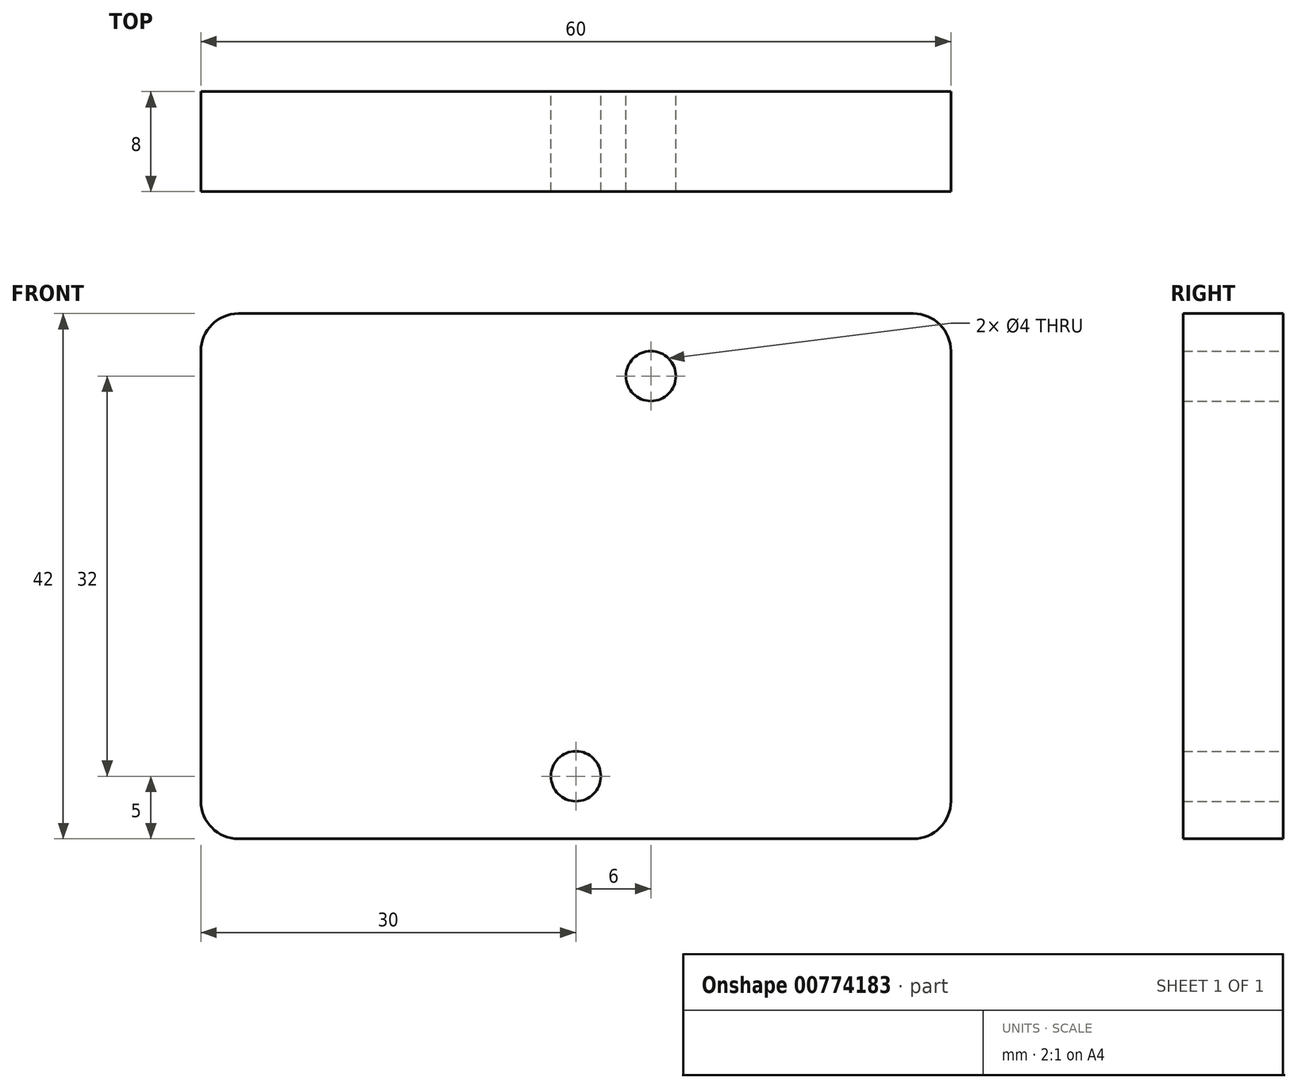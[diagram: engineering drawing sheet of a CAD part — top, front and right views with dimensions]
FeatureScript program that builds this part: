
annotation { "Feature Type Name" : "Feature", "Feature Type Description" : "" }
export const myFeature = defineFeature(function(context is Context, id is Id, definition is map)
    precondition{}
    {
        {
            var Q0;
            Q0=qCreatedBy(makeId("Front.planeOp"),FACE);
            var sketch = newSketch(context, id + "F0", { "sketchPlane" : qUnion([Q0])});
            skLineSegment(sketch, "E0.bottom", {"start": v(11.5, -11.5) * mm, "end": v(-11.5, -11.5) * mm});
            skLineSegment(sketch, "E0.top", {"start": v(11.5, 11.5) * mm, "end": v(-11.5, 11.5) * mm});
            skLineSegment(sketch, "E0.left", {"start": v(11.5, -11.5) * mm, "end": v(11.5, 11.5) * mm});
            skLineSegment(sketch, "E0.right", {"start": v(-11.5, -11.5) * mm, "end": v(-11.5, 11.5) * mm});
            skPoint(sketch, "E0.middle", {"position": v(0, 0) * mm});
            skLineSegment(sketch, "E1", {"start": v(11.5, 11.5) * mm, "end": v(11.5, 7.5) * mm});
            skLineSegment(sketch, "E2", {"start": v(11.5, 7.5) * mm, "end": v(16.5, 7.5) * mm});
            skLineSegment(sketch, "E3", {"start": v(16.5, 7.5) * mm, "end": v(16.5, 4.7) * mm});
            skLineSegment(sketch, "E4", {"start": v(16.5, 4.7) * mm, "end": v(11.5, 4.7) * mm});
            skLineSegment(sketch, "E5", {"start": v(-11.5, 11.5) * mm, "end": v(-11.5, 7.5) * mm});
            skLineSegment(sketch, "E6", {"start": v(-11.5, 7.5) * mm, "end": v(-16.5, 7.5) * mm});
            skLineSegment(sketch, "E7", {"start": v(-16.5, 7.5) * mm, "end": v(-16.5, 4.7) * mm});
            skLineSegment(sketch, "E8", {"start": v(-16.5, 4.7) * mm, "end": v(-11.5, 4.7) * mm});
            skSolve(sketch);
        }
        {
            var Q0;
            {var subQ2=sQuery(id+"F0.wireOp",EDGE,"E2");var subQ4=sQuery(id+"F0.wireOp",EDGE,"E0.bottom");var subQ11=sQuery(id+"F0.wireOp",EDGE,"E6");Q0=qUnion([makeQuery(id+"F0.imprint","IMPRINT",FACE,{"disambiguationData":[TD([[makeQuery(id+"F0.imprint","IMPRINT",EDGE,{"derivedFrom":subQ2}),-1.0]])]}),makeQuery(id+"F0.imprint","IMPRINT",FACE,{"disambiguationData":[TD([[makeQuery(id+"F0.imprint","IMPRINT",EDGE,{"derivedFrom":subQ11}),1.0]])]}),makeQuery(id+"F0.imprint","IMPRINT",FACE,{"disambiguationData":[TD([[makeQuery(id+"F0.imprint","IMPRINT",EDGE,{"derivedFrom":subQ4}),-1.0]])]})]);}
            extrude(context, id + "F1", {"entities" : qUnion([Q0]), "endBound" : BoundingType.SYMMETRIC, "depth" : 12.6 * mm, "offsetDistance" : 25 * mm});
        }
        {
            var Q0;
            Q0=qCreatedBy(makeId("Front.planeOp"),FACE);
            var sketch = newSketch(context, id + "F2", { "sketchPlane" : qUnion([Q0])});
            skLineSegment(sketch, "E9.bottom", {"start": v(23, -11.5) * mm, "end": v(-23, -11.5) * mm});
            skLineSegment(sketch, "E9.top", {"start": v(23, 11.5) * mm, "end": v(-23, 11.5) * mm});
            skLineSegment(sketch, "E9.left", {"start": v(23, -11.5) * mm, "end": v(23, 11.5) * mm});
            skLineSegment(sketch, "E9.right", {"start": v(-23, -11.5) * mm, "end": v(-23, 11.5) * mm});
            skPoint(sketch, "E9.middle", {"position": v(0, 0) * mm});
            skSolve(sketch);
        }
        {
            var Q0;
            Q0=qSketchRegion(id+"F2",true);
            extrude(context, id + "F3", {"entities" : qUnion([Q0]), "depth" : 16 * mm, "offsetDistance" : 25 * mm});
        }
        {
            var Q0;
            Q0=makeQuery(id+"F3.opExtrude","SWEPT_BODY",BODY,{"disambiguationData":[OSD([sQuery(id+"F2.wireOp",EDGE,"E9.bottom"),sQuery(id+"F2.wireOp",EDGE,"E9.top"),sQuery(id+"F2.wireOp",EDGE,"E9.left"),sQuery(id+"F2.wireOp",EDGE,"E9.right")])]});
            transform(context, id + "F4", {"entities" : qUnion([Q0]), "transformType" : TransformType.TRANSLATION_3D, "dx" : 0 * mm, "dy" : 9.75 * mm, "dz" : 0 * mm, "makeCopy" : false});
        }
        {
            var Q0;
            Q0=qCreatedBy(makeId("Front.planeOp"),FACE);
            var sketch = newSketch(context, id + "F5", { "sketchPlane" : qUnion([Q0])});
            skLineSegment(sketch, "E10", {"start": v(0, 0) * mm, "end": v(11.5, 0) * mm});
            skLineSegment(sketch, "E11", {"start": v(11.5, 0) * mm, "end": v(11.5, -4) * mm});
            skLineSegment(sketch, "E12", {"start": v(11.5, -4) * mm, "end": v(15.5, -4) * mm});
            skLineSegment(sketch, "E13", {"start": v(15.5, -4) * mm, "end": v(15.5, -11.5) * mm});
            skLineSegment(sketch, "E14", {"start": v(15.5, -11.5) * mm, "end": v(11.5, -11.5) * mm});
            skLineSegment(sketch, "E15", {"start": v(11.5, -11.5) * mm, "end": v(11.5, -4) * mm});
            skSolve(sketch);
        }
        {
            var Q0;
            Q0=qSketchRegion(id+"F5",true);
            extrude(context, id + "F6", {"entities" : qUnion([Q0]), "depth" : 25 * mm, "offsetDistance" : 25 * mm});
        }
        {
            var Q0;
            Q0=makeQuery(id+"F6.opExtrude","SWEPT_BODY",BODY,{"disambiguationData":[OSD([sQuery(id+"F5.wireOp",EDGE,"E12"),sQuery(id+"F5.wireOp",EDGE,"E13"),sQuery(id+"F5.wireOp",EDGE,"E14"),sQuery(id+"F5.wireOp",EDGE,"E15")])]});
            transform(context, id + "F7", {"entities" : qUnion([Q0]), "transformType" : TransformType.TRANSLATION_3D, "dx" : 0 * mm, "dy" : 4 * mm, "dz" : 0 * mm, "makeCopy" : false});
        }
        {
            var Q0;
            Q0=makeQuery(id+"F6.opExtrude","SWEPT_BODY",BODY,{"disambiguationData":[OSD([sQuery(id+"F5.wireOp",EDGE,"E12"),sQuery(id+"F5.wireOp",EDGE,"E13"),sQuery(id+"F5.wireOp",EDGE,"E14"),sQuery(id+"F5.wireOp",EDGE,"E15")])]});
            var Q1;
            Q1=makeQuery(id+"F1.opExtrude","SWEPT_BODY",BODY,{"disambiguationData":[OSD([sQuery(id+"F0.wireOp",EDGE,"E0.bottom"),sQuery(id+"F0.wireOp",EDGE,"E0.top"),sQuery(id+"F0.wireOp",EDGE,"E0.left"),sQuery(id+"F0.wireOp",EDGE,"E0.right"),sQuery(id+"F0.wireOp",EDGE,"E2"),sQuery(id+"F0.wireOp",EDGE,"E3"),sQuery(id+"F0.wireOp",EDGE,"E4"),sQuery(id+"F0.wireOp",EDGE,"E6"),sQuery(id+"F0.wireOp",EDGE,"E7"),sQuery(id+"F0.wireOp",EDGE,"E8")])]});
            var Q2;
            Q2=makeQuery(id+"F3.opExtrude","SWEPT_BODY",BODY,{"disambiguationData":[OSD([sQuery(id+"F2.wireOp",EDGE,"E9.bottom"),sQuery(id+"F2.wireOp",EDGE,"E9.top"),sQuery(id+"F2.wireOp",EDGE,"E9.left"),sQuery(id+"F2.wireOp",EDGE,"E9.right")])]});
            booleanBodies(context, id + "F8", {"operationType" : BooleanOperationType.SUBTRACTION, "tools" : qUnion([Q0, Q1]), "targets" : qUnion([Q2])});
        }
        {
            var Q0;
            Q0=makeQuery(id+"F3.opExtrude","CAP_EDGE",EDGE,{"disambiguationData":[OSD([sQuery(id+"F2.wireOp",EDGE,"E9.right")])],"isStart":false});
            var Q1;
            Q1=makeQuery(id+"F3.opExtrude","CAP_EDGE",EDGE,{"disambiguationData":[OSD([sQuery(id+"F2.wireOp",EDGE,"E9.left")])],"isStart":false});
            var Q2;
            Q2=makeQuery(id+"F3.opExtrude","SWEPT_EDGE",EDGE,{"disambiguationData":[OSD([sQuery(id+"F2.wireOp",EDGE,"E9.top"),sQuery(id+"F2.wireOp",EDGE,"E9.left")])]});
            var Q3;
            Q3=makeQuery(id+"F3.opExtrude","SWEPT_EDGE",EDGE,{"disambiguationData":[OSD([sQuery(id+"F2.wireOp",EDGE,"E9.top"),sQuery(id+"F2.wireOp",EDGE,"E9.right")])]});
            var Q4;
            {var subQ1=sQuery(id+"F2.wireOp",EDGE,"E9.right");var subQ2=sQuery(id+"F2.wireOp",EDGE,"E9.top");Q4=makeQuery(id+"F8.opBoolean","SPLIT",EDGE,{"disambiguationData":[TD([makeQuery(id+"F3.opExtrude","SWEPT_FACE",FACE,{"disambiguationData":[OSD([subQ1])]})])],"derivedFrom":makeQuery(id+"F3.opExtrude","CAP_EDGE",EDGE,{"disambiguationData":[OSD([subQ2])],"isStart":false})});}
            var Q5;
            {var subQ1=sQuery(id+"F2.wireOp",EDGE,"E9.left");var subQ2=sQuery(id+"F2.wireOp",EDGE,"E9.top");Q5=makeQuery(id+"F8.opBoolean","SPLIT",EDGE,{"disambiguationData":[TD([makeQuery(id+"F3.opExtrude","SWEPT_FACE",FACE,{"disambiguationData":[OSD([subQ1])]})])],"derivedFrom":makeQuery(id+"F3.opExtrude","CAP_EDGE",EDGE,{"disambiguationData":[OSD([subQ2])],"isStart":false})});}
            var Q6;
            Q6=makeQuery(id+"F3.opExtrude","SWEPT_EDGE",EDGE,{"disambiguationData":[OSD([sQuery(id+"F2.wireOp",EDGE,"E9.bottom"),sQuery(id+"F2.wireOp",EDGE,"E9.left")])]});
            var Q7;
            {var subQ0=sQuery(id+"F2.wireOp",EDGE,"E9.bottom");var subQ1=sQuery(id+"F2.wireOp",EDGE,"E9.left");Q7=makeQuery(id+"F8.opBoolean","SPLIT",EDGE,{"disambiguationData":[TD([makeQuery(id+"F3.opExtrude","SWEPT_FACE",FACE,{"disambiguationData":[OSD([subQ1])]})])],"derivedFrom":makeQuery(id+"F3.opExtrude","CAP_EDGE",EDGE,{"disambiguationData":[OSD([subQ0])],"isStart":false})});}
            var Q8;
            Q8=makeQuery(id+"F3.opExtrude","SWEPT_EDGE",EDGE,{"disambiguationData":[OSD([sQuery(id+"F2.wireOp",EDGE,"E9.bottom"),sQuery(id+"F2.wireOp",EDGE,"E9.right")])]});
            var Q9;
            {var subQ1=sQuery(id+"F2.wireOp",EDGE,"E9.bottom");var subQ2=sQuery(id+"F2.wireOp",EDGE,"E9.right");Q9=makeQuery(id+"F8.opBoolean","SPLIT",EDGE,{"disambiguationData":[TD([makeQuery(id+"F3.opExtrude","SWEPT_FACE",FACE,{"disambiguationData":[OSD([subQ2])]})])],"derivedFrom":makeQuery(id+"F3.opExtrude","CAP_EDGE",EDGE,{"disambiguationData":[OSD([subQ1])],"isStart":false})});}
            fillet(context, id + "F9", {"entities" : qUnion([Q0, Q1, Q2, Q3, Q4, Q5, Q6, Q7, Q8, Q9]), "radius" : 1.5 * mm, "tangentPropagation" : true, "allowEdgeOverflow" : false});
        }
        {
            var Q0;
            Q0=qCreatedBy(makeId("Front.planeOp"),FACE);
            var sketch = newSketch(context, id + "F10", { "sketchPlane" : qUnion([Q0])});
            skLineSegment(sketch, "E16.bottom", {"start": v(23, -21) * mm, "end": v(-23, -21) * mm});
            skLineSegment(sketch, "E16.top", {"start": v(23, 21) * mm, "end": v(-23, 21) * mm});
            skLineSegment(sketch, "E16.left", {"start": v(23, -21) * mm, "end": v(23, 21) * mm});
            skLineSegment(sketch, "E16.right", {"start": v(-23, -21) * mm, "end": v(-23, 21) * mm});
            skPoint(sketch, "E16.middle", {"position": v(0, 0) * mm});
            skLineSegment(sketch, "E17", {"start": v(0, 0) * mm, "end": v(0, 16) * mm});
            skLineSegment(sketch, "E18", {"start": v(0, 16) * mm, "end": v(18, 16) * mm});
            skLineSegment(sketch, "E19", {"start": v(0, 16) * mm, "end": v(-18, 16) * mm});
            skLineSegment(sketch, "E20", {"start": v(0, 0) * mm, "end": v(0, -16) * mm});
            skLineSegment(sketch, "E21", {"start": v(0, -16) * mm, "end": v(18, -16) * mm});
            skLineSegment(sketch, "E22", {"start": v(0, -16) * mm, "end": v(-18, -16) * mm});
            skLineSegment(sketch, "E23", {"start": v(-18, 16) * mm, "end": v(-18, 18) * mm});
            skLineSegment(sketch, "E24", {"start": v(18, 16) * mm, "end": v(18, 14) * mm});
            skLineSegment(sketch, "E25", {"start": v(-18, -16) * mm, "end": v(-18, -14) * mm});
            skLineSegment(sketch, "E26", {"start": v(18, -16) * mm, "end": v(18, -18) * mm});
            skArc(sketch, "E27", {"start": v(-18, 18) * mm, "mid": v(-20, 16) * mm, "end": v(-18, 14) * mm});
            skArc(sketch, "E28", {"start": v(18, 14) * mm, "mid": v(20, 16) * mm, "end": v(18, 18) * mm});
            skArc(sketch, "E29", {"start": v(-18, -14) * mm, "mid": v(-20, -16) * mm, "end": v(-18, -18) * mm});
            skArc(sketch, "E30", {"start": v(18, -18) * mm, "mid": v(20, -16) * mm, "end": v(18, -14) * mm});
            skLineSegment(sketch, "E31", {"start": v(-18, 18) * mm, "end": v(18, 18) * mm});
            skLineSegment(sketch, "E32", {"start": v(-18, 14) * mm, "end": v(18, 14) * mm});
            skLineSegment(sketch, "E33", {"start": v(-18, -14) * mm, "end": v(18, -14) * mm});
            skLineSegment(sketch, "E34", {"start": v(-18, -18) * mm, "end": v(18, -18) * mm});
            skSolve(sketch);
        }
        {
            var Q0;
            Q0=qSketchRegion(id+"F10",true);
            extrude(context, id + "F11", {"entities" : qUnion([Q0]), "depth" : 3 * mm, "offsetDistance" : 25 * mm});
        }
        {
            var Q0;
            Q0=makeQuery(id+"F11.opExtrude","SWEPT_BODY",BODY,{"disambiguationData":[OSD([sQuery(id+"F10.wireOp",EDGE,"E16.bottom"),sQuery(id+"F10.wireOp",EDGE,"E16.top"),sQuery(id+"F10.wireOp",EDGE,"E16.left"),sQuery(id+"F10.wireOp",EDGE,"E16.right"),sQuery(id+"F10.wireOp",EDGE,"E27"),sQuery(id+"F10.wireOp",EDGE,"E28"),sQuery(id+"F10.wireOp",EDGE,"E29"),sQuery(id+"F10.wireOp",EDGE,"E30"),sQuery(id+"F10.wireOp",EDGE,"E31"),sQuery(id+"F10.wireOp",EDGE,"E32"),sQuery(id+"F10.wireOp",EDGE,"E33"),sQuery(id+"F10.wireOp",EDGE,"E34")])]});
            transform(context, id + "F12", {"entities" : qUnion([Q0]), "transformType" : TransformType.TRANSLATION_3D, "dx" : 0 * mm, "dy" : 12 * mm, "dz" : 0 * mm, "makeCopy" : false});
        }
        {
            var Q0;
            Q0=makeQuery(id+"F11.opExtrude","SWEPT_EDGE",EDGE,{"disambiguationData":[OSD([sQuery(id+"F10.wireOp",EDGE,"E16.top"),sQuery(id+"F10.wireOp",EDGE,"E16.right")])]});
            var Q1;
            Q1=makeQuery(id+"F11.opExtrude","SWEPT_EDGE",EDGE,{"disambiguationData":[OSD([sQuery(id+"F10.wireOp",EDGE,"E16.top"),sQuery(id+"F10.wireOp",EDGE,"E16.left")])]});
            var Q2;
            Q2=makeQuery(id+"F11.opExtrude","SWEPT_EDGE",EDGE,{"disambiguationData":[OSD([sQuery(id+"F10.wireOp",EDGE,"E16.bottom"),sQuery(id+"F10.wireOp",EDGE,"E16.left")])]});
            var Q3;
            Q3=makeQuery(id+"F11.opExtrude","SWEPT_EDGE",EDGE,{"disambiguationData":[OSD([sQuery(id+"F10.wireOp",EDGE,"E16.bottom"),sQuery(id+"F10.wireOp",EDGE,"E16.right")])]});
            fillet(context, id + "F13", {"entities" : qUnion([Q0, Q1, Q2, Q3]), "radius" : 3 * mm, "tangentPropagation" : true, "allowEdgeOverflow" : false});
        }
        {
            var Q0;
            Q0=qCreatedBy(makeId("Front.planeOp"),FACE);
            var sketch = newSketch(context, id + "F14", { "sketchPlane" : qUnion([Q0])});
            skLineSegment(sketch, "E35.bottom", {"start": v(30, -21) * mm, "end": v(-30, -21) * mm});
            skLineSegment(sketch, "E35.top", {"start": v(30, 21) * mm, "end": v(-30, 21) * mm});
            skLineSegment(sketch, "E35.left", {"start": v(30, -21) * mm, "end": v(30, 21) * mm});
            skLineSegment(sketch, "E35.right", {"start": v(-30, -21) * mm, "end": v(-30, 21) * mm});
            skPoint(sketch, "E35.middle", {"position": v(0, 0) * mm});
            skLineSegment(sketch, "E36", {"start": v(0, 0) * mm, "end": v(0, 16) * mm});
            skLineSegment(sketch, "E37", {"start": v(0, 0) * mm, "end": v(0, -16) * mm});
            skLineSegment(sketch, "E38", {"start": v(0, 16) * mm, "end": v(6, 16) * mm});
            skCircle(sketch, "E39", {"center": v(6, 16) * mm, "radius": 2 * mm});
            skCircle(sketch, "E40", {"center": v(0, -16) * mm, "radius": 2 * mm});
            skSolve(sketch);
        }
        {
            var Q0;
            Q0 = qSketchRegion(id + "F14", true);
            extrude(context, id + "F15", {"entities" : qUnion([Q0]), "depth" : 8 * mm, "offsetDistance" : 25 * mm});
        }
        {
            var Q0;
            Q0=makeQuery(id+"F15.opExtrude","SWEPT_EDGE",EDGE,{"disambiguationData":[OSD([sQuery(id+"F14.wireOp",EDGE,"E35.bottom"),sQuery(id+"F14.wireOp",EDGE,"E35.left")])]});
            var Q1;
            Q1=makeQuery(id+"F15.opExtrude","SWEPT_EDGE",EDGE,{"disambiguationData":[OSD([sQuery(id+"F14.wireOp",EDGE,"E35.bottom"),sQuery(id+"F14.wireOp",EDGE,"E35.right")])]});
            var Q2;
            Q2=makeQuery(id+"F15.opExtrude","SWEPT_EDGE",EDGE,{"disambiguationData":[OSD([sQuery(id+"F14.wireOp",EDGE,"E35.top"),sQuery(id+"F14.wireOp",EDGE,"E35.right")])]});
            var Q3;
            Q3=makeQuery(id+"F15.opExtrude","SWEPT_EDGE",EDGE,{"disambiguationData":[OSD([sQuery(id+"F14.wireOp",EDGE,"E35.top"),sQuery(id+"F14.wireOp",EDGE,"E35.left")])]});
            fillet(context, id + "F16", {"entities" : qUnion([Q0, Q1, Q2, Q3]), "radius" : 3 * mm, "tangentPropagation" : true, "allowEdgeOverflow" : false});
        }
        {
            var Q0;
            Q0=makeQuery(id+"F3.opExtrude","SWEPT_BODY",BODY,{"disambiguationData":[OSD([sQuery(id+"F2.wireOp",EDGE,"E9.bottom"),sQuery(id+"F2.wireOp",EDGE,"E9.top"),sQuery(id+"F2.wireOp",EDGE,"E9.left"),sQuery(id+"F2.wireOp",EDGE,"E9.right")])]});
            var Q1;
            Q1=makeQuery(id+"F11.opExtrude","SWEPT_BODY",BODY,{"disambiguationData":[OSD([sQuery(id+"F10.wireOp",EDGE,"E16.bottom"),sQuery(id+"F10.wireOp",EDGE,"E16.top"),sQuery(id+"F10.wireOp",EDGE,"E16.left"),sQuery(id+"F10.wireOp",EDGE,"E16.right"),sQuery(id+"F10.wireOp",EDGE,"E27"),sQuery(id+"F10.wireOp",EDGE,"E28"),sQuery(id+"F10.wireOp",EDGE,"E29"),sQuery(id+"F10.wireOp",EDGE,"E30"),sQuery(id+"F10.wireOp",EDGE,"E31"),sQuery(id+"F10.wireOp",EDGE,"E32"),sQuery(id+"F10.wireOp",EDGE,"E33"),sQuery(id+"F10.wireOp",EDGE,"E34")])]});
            deleteBodies(context, id + "F17", {"entities" : qUnion([Q0, Q1])});
        }
    });
